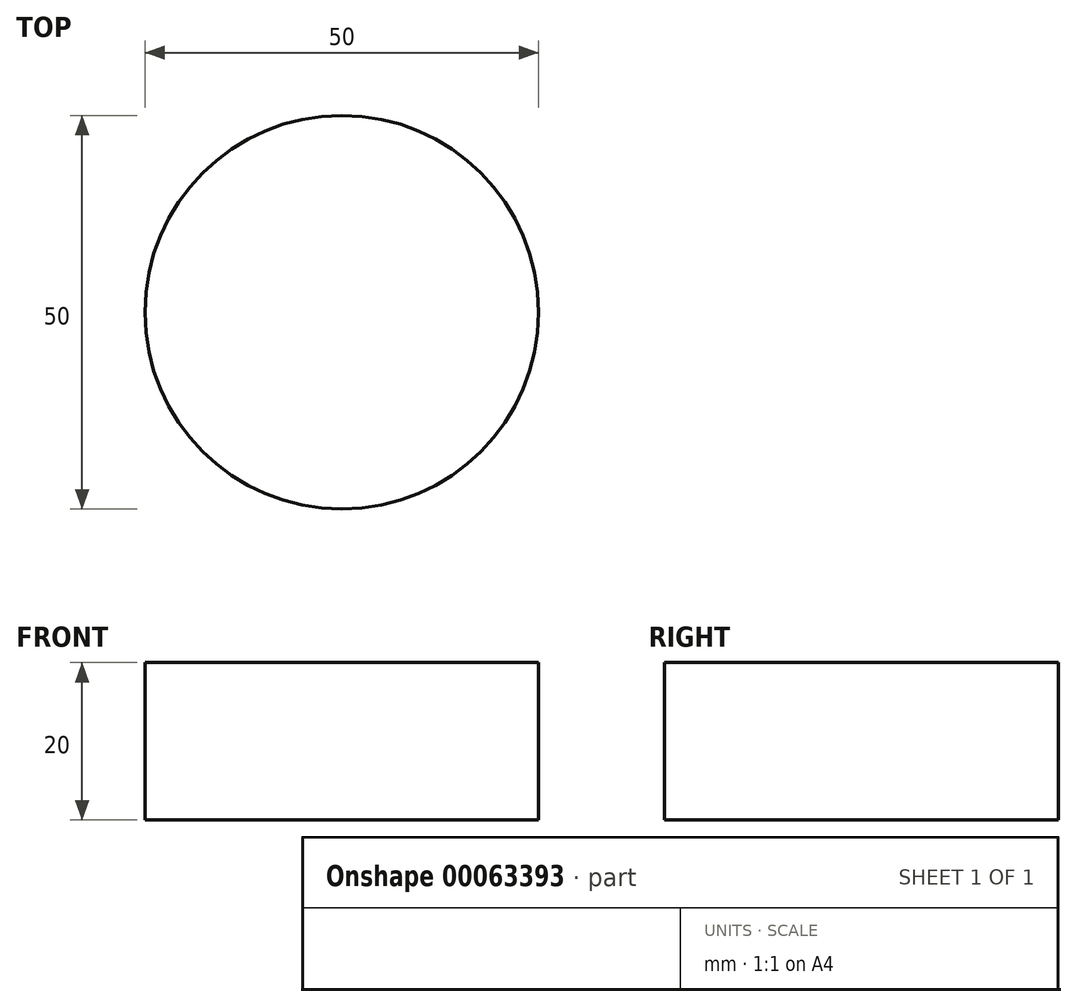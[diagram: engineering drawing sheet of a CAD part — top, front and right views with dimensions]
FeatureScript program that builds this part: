
annotation { "Feature Type Name" : "Feature", "Feature Type Description" : "" }
export const myFeature = defineFeature(function(context is Context, id is Id, definition is map)
    precondition{}
    {
        {
            var Q0;
            Q0=qCreatedBy(makeId("Top.planeOp"),FACE);
            var sketch = newSketch(context, id + "F0", { "sketchPlane" : qUnion([Q0])});
            skCircle(sketch, "E0", {"center": v(0, 0) * mm, "radius": 25 * mm});
            skSolve(sketch);
        }
        {
            var Q0;
            Q0=makeQuery(id+"F0.imprint","IMPRINT",FACE,{"disambiguationData":[TD([[makeQuery(id+"F0.imprint","IMPRINT",EDGE,{"derivedFrom":sQuery(id+"F0.wireOp",EDGE,"E0")}),1.0]])]});
            extrude(context, id + "F1", {"entities" : qUnion([Q0]), "depth" : 20 * mm});
        }
    });
